# Revit family: WH1845B
name_source: partatom
category: Mechanical Equipment
revit_build: Autodesk Revit MEP 2016 (Build: 20150220_1215(x64)
units: mm (PartAtom-declared; Revit-internal decimal feet)

## family parameters
Cut with Voids When Loaded = No
Host = Face
OmniClass Number = 23.40.20.21.21
OmniClass Title = Toilet Paper Dispensers
Part Type = Normal
Room Calculation Point = No
Round Connector Dimension = Use Diameter
Shared = Yes

## types (1)
- WH1845B
    Amperage = 0
    CW Connection = No
    Default Elevation = 0 "
    Description = Ligature Resistant Spindle Button Semi-Recessed Toilet Paper Holder
    HW Connection = No
    Manufacturer = Whitehall Mfg
    Material = Stainless Steel
    Model = WH1845B
    OVERALL DEPTH = 0.75
    OVERALL SIZE HEIGHT = 7.625
    OVERALL SIZE WIDTH = 8.75
    Revised Date = 06/26/19
    Tempered Water Connection = No
    URL = https://www.whitehallmfg.com
    Vent Connection = No
    Voltage = 0
    Waste Connection = No

## geometry (parser evidence)
native form markers: Sweep x13
no freeform markers — native parametric forms only
